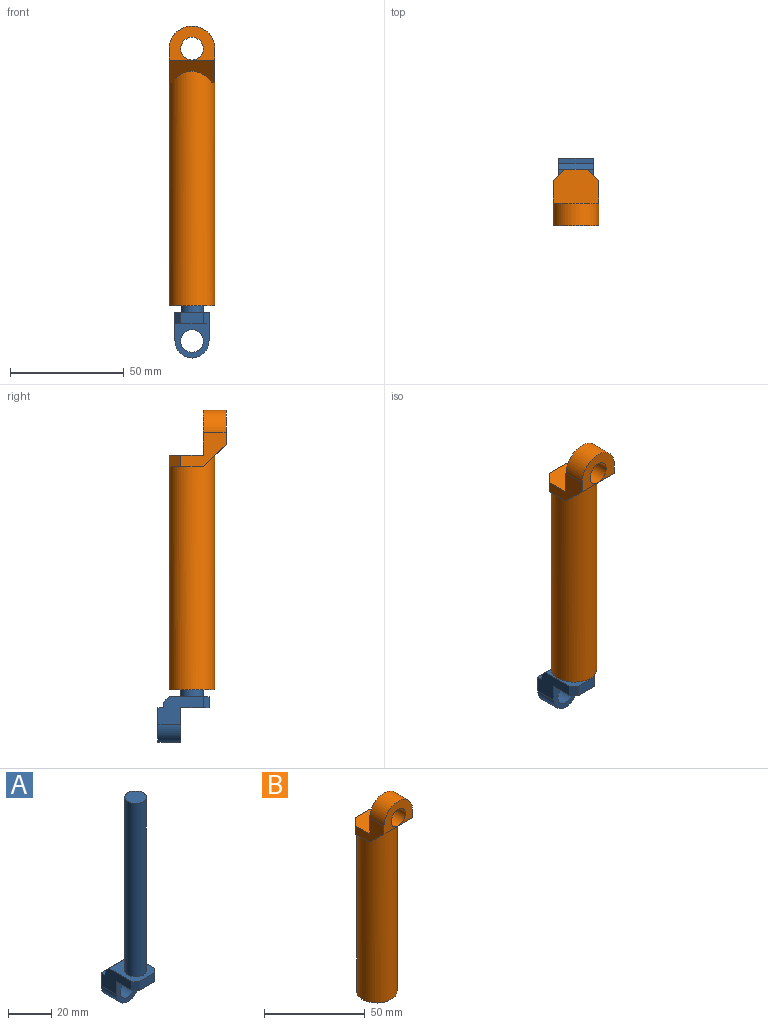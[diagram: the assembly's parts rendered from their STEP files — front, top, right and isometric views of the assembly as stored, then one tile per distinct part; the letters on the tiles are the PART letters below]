
ASSEMBLY  parts=2 mates=1
PART A: 16 faces, bbox 15x22.5x118.1 mm
  f0: plane 20x12.5mm, normal (1,0,0), area 159.4mm2, adj f4,f5,f8,f9,f10,f11,f12,f13
  f1: cylinder r=5mm len=10mm, axis (0,-1,0), area 314.2mm2, adj f11,f12
  f2: plane 10x10mm, normal (0,0,1), area 78.5mm2, adj f3
  f3: cylinder r=5mm len=98.08mm, axis (0,0,1), area 3081.2mm2, adj f2,f5
  f4: plane 15x12.5mm, normal (0,0,-1), area 181.3mm2, adj f0,f6,f7,f12,f14,f15
  f5: plane 17.5x15mm, normal (0,0,1), area 177.7mm2, adj f0,f3,f6,f7,f13,f14,f15
  f6: plane 20x12.5mm, normal (-1,0,0), area 159.4mm2, adj f4,f5,f8,f9,f10,f11,f12,f13
  f7: plane 10x5mm, normal (0,-1,0), area 50mm2, adj f4,f5,f14,f15
  f8: plane 15x2.5mm, normal (0,1,0), area 37.5mm2, adj f0,f6,f9,f13
  f9: plane 15x2.5mm, normal (0,0,1), area 37.5mm2, adj f0,f6,f8,f11
  f10: cylinder r=7.5mm len=15mm, axis (0,-1,0), area 235.6mm2, adj f0,f6,f11,f12
  f11: plane 15x15mm, normal (0,1,0), area 122.3mm2, adj f0,f1,f6,f9,f10
  f12: plane 15x15mm, normal (0,-1,0), area 122.3mm2, adj f0,f1,f4,f6,f10
  f13: plane 15x2.5mm, normal (0,0.71,0.71), area 53mm2, adj f0,f5,f6,f8
  f14: plane 5x2.5mm, normal (0.71,-0.71,0), area 17.7mm2, adj f0,f4,f5,f7
  f15: plane 5x2.5mm, normal (-0.71,-0.71,0), area 17.7mm2, adj f4,f5,f6,f7
PART B: 19 faces, bbox 20x25x123.1 mm
  f0: plane 20x15mm, normal (1,0,0), area 150mm2, adj f1,f6,f9,f12,f14,f15,f16,f17
  f1: plane 20x15mm, normal (0,0,1), area 275mm2, adj f0,f10,f11,f15,f17,f18
  f2: cylinder r=10mm len=103.09mm, axis (0,0,1), area 6230.9mm2, adj f4,f6,f7,f8,f9,f16
  f3: cylinder r=5mm len=98.08mm, axis (0,0,1), area 3081.2mm2, adj f4,f5
  f4: plane 20x20mm, normal (0,0,-1), area 235.6mm2, adj f2,f3
  f5: plane 10x10mm, normal (0,0,-1), area 78.5mm2, adj f3
  f6: plane 10x10mm, normal (0,0,-1), area 9mm2, adj f0,f2,f11,f17
  f7: plane 10x10mm, normal (0,0,-1), area 9mm2, adj f2,f10,f11,f18
  f8: plane 5x1.34mm, normal (0,0,-1), area 2.2mm2, adj f2,f10,f16
  f9: plane 5x1.34mm, normal (0,0,-1), area 2.2mm2, adj f0,f2,f16
  f10: plane 20x15mm, normal (-1,0,0), area 150mm2, adj f1,f7,f8,f12,f14,f15,f16,f18
  f11: plane 10x5mm, normal (0,1,0), area 50mm2, adj f1,f6,f7,f17,f18
  f12: cylinder r=10mm len=20mm, axis (0,1,0), area 314.2mm2, adj f0,f10,f14,f15
  f13: cylinder r=5mm len=10mm, axis (0,1,0), area 314.2mm2, adj f14,f15
  f14: plane 20x15mm, normal (0,-1,0), area 178.5mm2, adj f0,f10,f12,f13,f16
  f15: plane 20x20mm, normal (0,1,0), area 278.5mm2, adj f0,f1,f10,f12,f13
  f16: plane 20x10mm, normal (0,-0.71,-0.71), area 196mm2, adj f0,f2,f8,f9,f10,f14
  f17: plane 5x5mm, normal (0.71,0.71,0), area 35.4mm2, adj f0,f1,f6,f11
  f18: plane 5x5mm, normal (-0.71,0.71,0), area 35.4mm2, adj f1,f7,f10,f11
PLACE A t=(113.39,5.15,12.91)mm
PLACE B t=(113.39,5.15,2.91)mm
MATE slider A.f3 <-> B.f2  axis (0,0,1) through (167.48,5.15,10.79)mm
